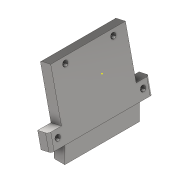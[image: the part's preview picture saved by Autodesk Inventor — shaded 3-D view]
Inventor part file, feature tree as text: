
AUTODESK INVENTOR PART (.ipt)
format: ipt  version: 2020.3 (Build 243373010, 373A)  size: 171,008 bytes
history: native  units: mm
features: sketch x5, extrude x4, projected_geometry x2, hole x1, fillet x1
ambient origin geometry x8: Origin, YZ Plane, XZ Plane, XY Plane, X Axis, Y Axis, Z Axis, Center Point
bodies: Body1 (feature_tree)
feature tree (13):
  extrude  "Extrusion8"  Depth=140.0mm
  sketch  "Sketch10"  dims[d40=70.0mm d41=38.692mm d42=0.0mm]
  extrude  "Extrusion9"  Depth=38.692mm TaperAngle=0.0deg
  extrude  "Extrusion10"  Depth=25.0mm
  sketch  "Sketch13"  dims[d49=10.0mm d50=0.0mm d51=6.917mm d52=16.0mm d53=10.025mm d54=6.025mm d55=90.0deg d56=21.1mm d57=20.594885mm d58=90.0deg d59=5.0mm]
  extrude  "Extrusion11"  Depth=140.0mm TaperAngle=0.0deg
  hole  "Hole1"  [1 undecoded]
  fillet  "Fillet3"  Radius=5.0mm
  sketch  "Sketch9"  dims[d37=190.0mm d38=0.0mm d39=140.0mm]
  sketch  "Sketch11"  dims[d44=25.0mm d45=25.0mm]
  projected_geometry  "Projected Loop4"
  sketch  "Sketch12"  dims[d46=140.0mm d47=25.807mm d48=0.0mm]
  projected_geometry  "Projected Loop5"
note: 1 required parameter value undecoded (feature->parameter linkage not recoverable at this tier; creation-order binding heuristic only, values carry confidence <= 0.55)
